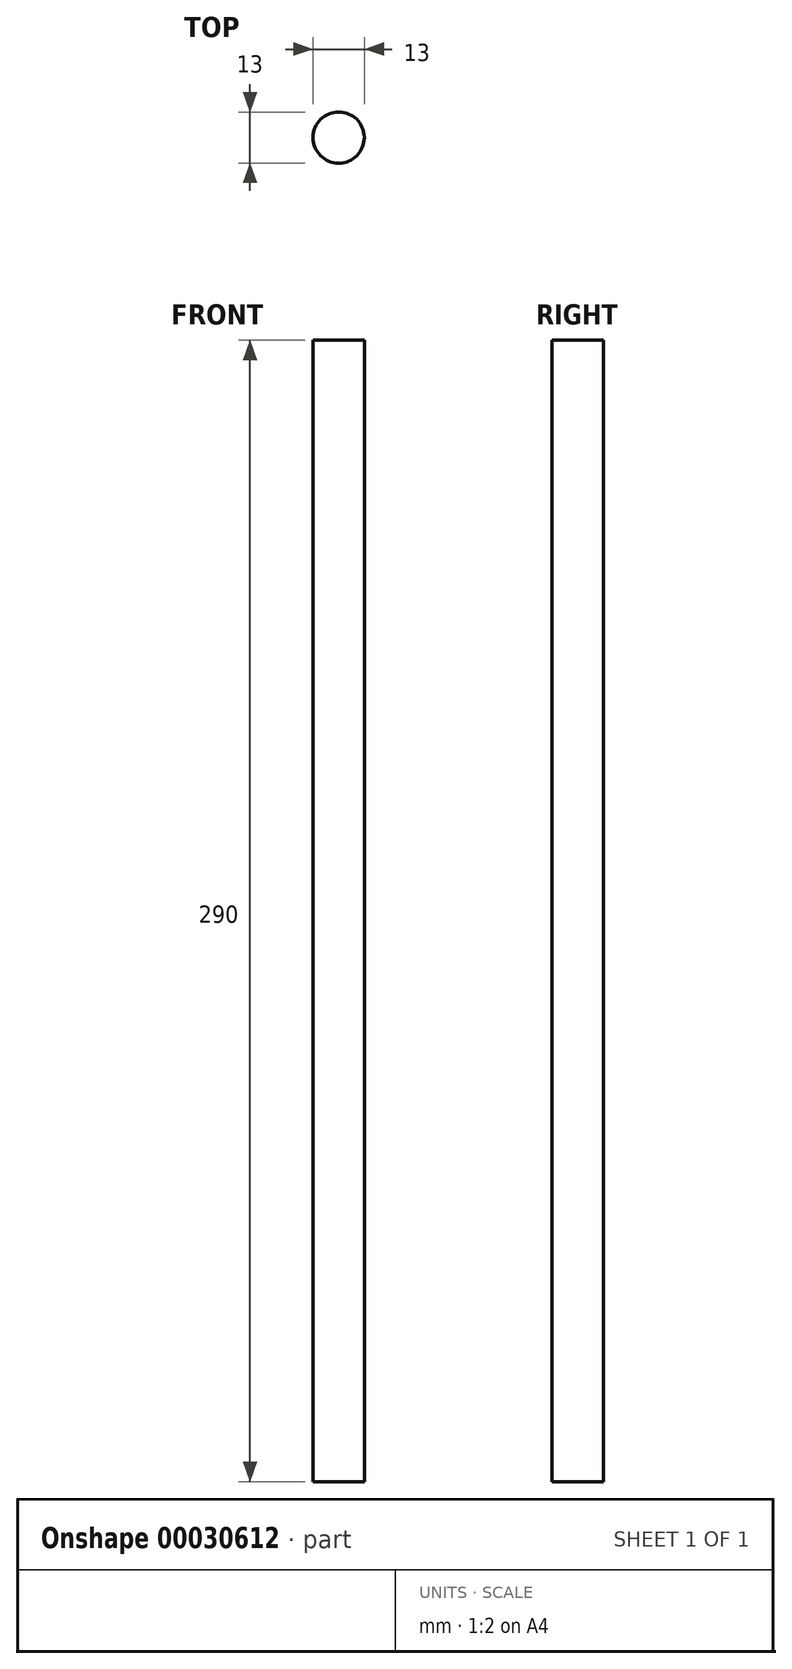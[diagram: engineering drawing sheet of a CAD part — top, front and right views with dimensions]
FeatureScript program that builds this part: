
annotation { "Feature Type Name" : "Feature", "Feature Type Description" : "" }
export const myFeature = defineFeature(function(context is Context, id is Id, definition is map)
    precondition{}
    {
        {
            var Q0;
            Q0=qCreatedBy(makeId("Top.planeOp"),FACE);
            var sketch = newSketch(context, id + "F0", { "sketchPlane" : qUnion([Q0])});
            skCircle(sketch, "E0", {"center": v(0, 0) * mm, "radius": 6.5 * mm});
            skSolve(sketch);
        }
        {
            var Q0;
            Q0=makeQuery(id+"F0.imprint","IMPRINT",FACE,{"disambiguationData":[TD([[makeQuery(id+"F0.imprint","IMPRINT",EDGE,{"derivedFrom":sQuery(id+"F0.wireOp",EDGE,"E0")}),1.0]])]});
            extrude(context, id + "F1", {"entities" : qUnion([Q0]), "depth" : 290 * mm});
        }
    });
